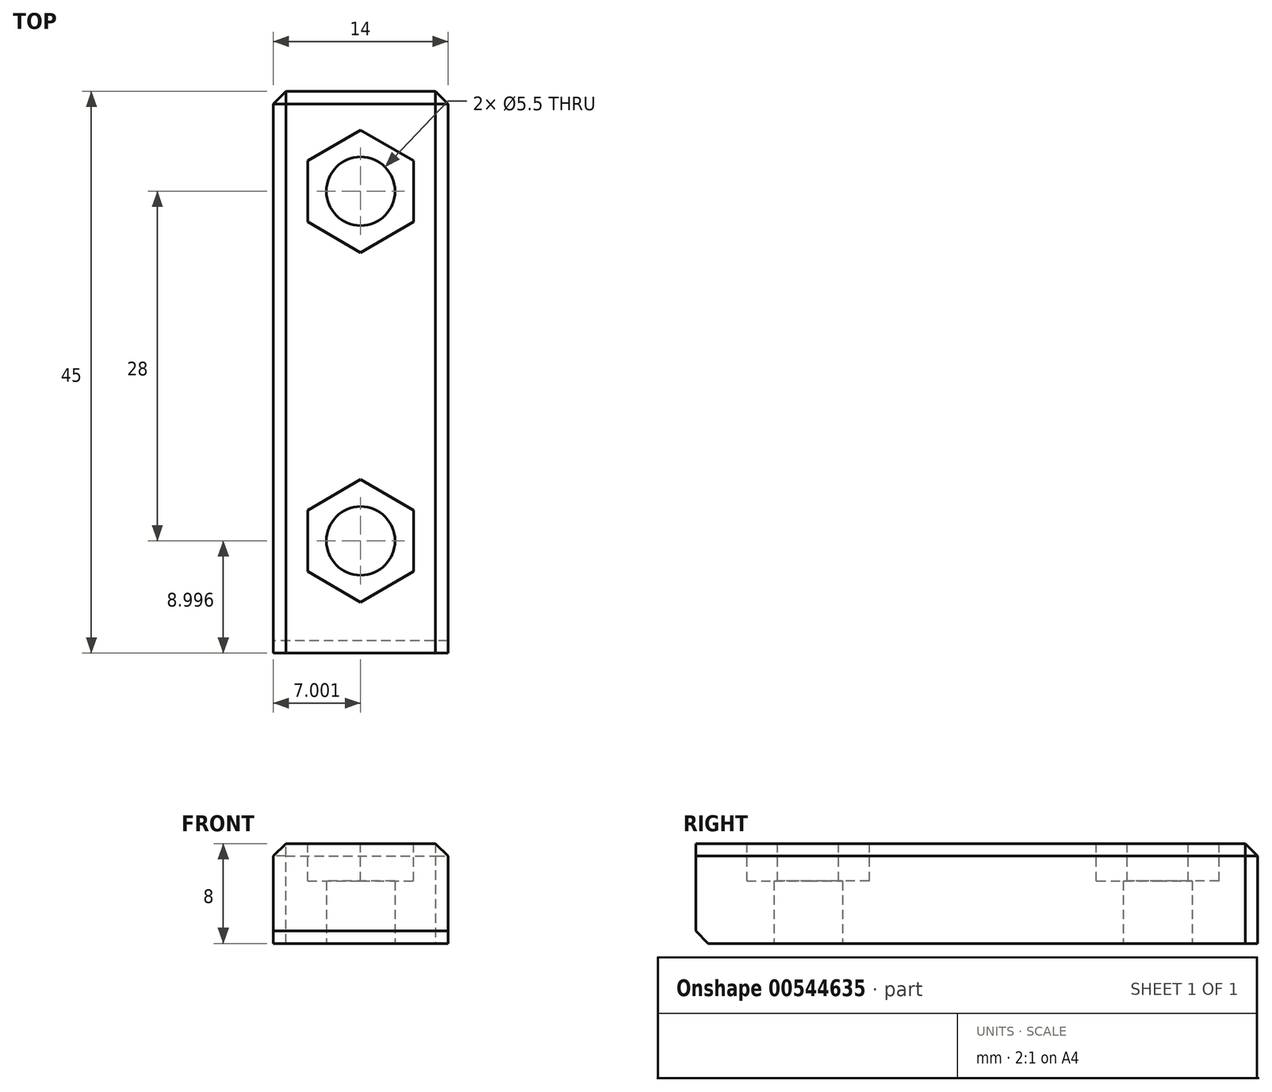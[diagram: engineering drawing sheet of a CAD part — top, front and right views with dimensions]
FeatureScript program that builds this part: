
annotation { "Feature Type Name" : "Feature", "Feature Type Description" : "" }
export const myFeature = defineFeature(function(context is Context, id is Id, definition is map)
    precondition{}
    {
        {
            var Q0;
            Q0=qCreatedBy(makeId("Top.planeOp"),FACE);
            var sketch = newSketch(context, id + "F0", { "sketchPlane" : qUnion([Q0])});
            skLineSegment(sketch, "E0.bottom", {"start": v(-22.78, 37.96) * mm, "end": v(-8.78, 37.96) * mm});
            skLineSegment(sketch, "E0.top", {"start": v(-22.78, -7.04) * mm, "end": v(-8.78, -7.04) * mm});
            skLineSegment(sketch, "E0.left", {"start": v(-22.78, 37.96) * mm, "end": v(-22.78, -7.04) * mm});
            skLineSegment(sketch, "E0.right", {"start": v(-8.78, 37.96) * mm, "end": v(-8.78, -7.04) * mm});
            skPoint(sketch, "E1", {"position": v(-15.78, -7.04) * mm});
            skCircle(sketch, "E2", {"center": v(-15.78, 1.96) * mm, "radius": 2.75 * mm});
            skCircle(sketch, "E3", {"center": v(-15.78, 29.96) * mm, "radius": 2.75 * mm});
            skSolve(sketch);
        }
        {
            var Q0;
            Q0=makeQuery(id+"F0.imprint","IMPRINT",FACE,{"disambiguationData":[TD([[makeQuery(id+"F0.imprint","IMPRINT",EDGE,{"derivedFrom":sQuery(id+"F0.wireOp",EDGE,"E0.bottom")}),-1.0]])]});
            extrude(context, id + "F1", {"entities" : qUnion([Q0]), "depth" : 8 * mm, "offsetDistance" : 25 * mm});
        }
        {
            var Q0;
            Q0=makeQuery(id+"F1.opExtrude","CAP_FACE",FACE,{"disambiguationData":[OSD([sQuery(id+"F0.wireOp",EDGE,"E0.bottom"),sQuery(id+"F0.wireOp",EDGE,"E0.top"),sQuery(id+"F0.wireOp",EDGE,"E0.left"),sQuery(id+"F0.wireOp",EDGE,"E0.right"),sQuery(id+"F0.wireOp",EDGE,"E2"),sQuery(id+"F0.wireOp",EDGE,"E3")])],"isStart":false});
            var sketch = newSketch(context, id + "F2", { "sketchPlane" : qUnion([Q0])});
            skCircle(sketch, "E4.cCircle", {"center": v(-15.78, 29.96) * mm, "radius": 4.25 * mm, "construction": true});
            skLineSegment(sketch, "E4.0", {"start": v(-11.53, 32.41) * mm, "end": v(-11.53, 27.5) * mm});
            skLineSegment(sketch, "E4.1", {"start": v(-11.53, 27.5) * mm, "end": v(-15.78, 25.05) * mm});
            skLineSegment(sketch, "E4.2", {"start": v(-15.78, 25.05) * mm, "end": v(-20.03, 27.5) * mm});
            skLineSegment(sketch, "E4.3", {"start": v(-20.03, 27.5) * mm, "end": v(-20.03, 32.41) * mm});
            skLineSegment(sketch, "E4.4", {"start": v(-20.03, 32.41) * mm, "end": v(-15.78, 34.86) * mm});
            skLineSegment(sketch, "E4.5", {"start": v(-15.78, 34.86) * mm, "end": v(-11.53, 32.41) * mm});
            skPoint(sketch, "E4.0.midPoint", {"position": v(-11.53, 29.96) * mm});
            skCircle(sketch, "E5.cCircle", {"center": v(-15.78, 1.96) * mm, "radius": 4.25 * mm, "construction": true});
            skLineSegment(sketch, "E5.0", {"start": v(-11.53, 4.41) * mm, "end": v(-11.53, -0.5) * mm});
            skLineSegment(sketch, "E5.1", {"start": v(-11.53, -0.5) * mm, "end": v(-15.78, -2.95) * mm});
            skLineSegment(sketch, "E5.2", {"start": v(-15.78, -2.95) * mm, "end": v(-20.03, -0.5) * mm});
            skLineSegment(sketch, "E5.3", {"start": v(-20.03, -0.5) * mm, "end": v(-20.03, 4.41) * mm});
            skLineSegment(sketch, "E5.4", {"start": v(-20.03, 4.41) * mm, "end": v(-15.78, 6.86) * mm});
            skLineSegment(sketch, "E5.5", {"start": v(-15.78, 6.86) * mm, "end": v(-11.53, 4.41) * mm});
            skPoint(sketch, "E5.0.midPoint", {"position": v(-11.53, 1.96) * mm});
            skSolve(sketch);
        }
        {
            var Q0;
            Q0 = qSketchRegion(id + "F2", true);
            extrude(context, id + "F3", {"entities" : qUnion([Q0]), "operationType" : NewBodyOperationType.REMOVE, "oppositeDirection" : true, "depth" : 3 * mm, "offsetDistance" : 25 * mm});
        }
        {
            var Q0;
            Q0=makeQuery(id+"F1.opExtrude","CAP_EDGE",EDGE,{"disambiguationData":[OSD([sQuery(id+"F0.wireOp",EDGE,"E0.bottom")])],"isStart":false});
            var Q1;
            Q1=makeQuery(id+"F1.opExtrude","SWEPT_EDGE",EDGE,{"disambiguationData":[OSD([sQuery(id+"F0.wireOp",EDGE,"E0.bottom"),sQuery(id+"F0.wireOp",EDGE,"E0.right")])]});
            var Q2;
            Q2=makeQuery(id+"F1.opExtrude","SWEPT_EDGE",EDGE,{"disambiguationData":[OSD([sQuery(id+"F0.wireOp",EDGE,"E0.bottom"),sQuery(id+"F0.wireOp",EDGE,"E0.left")])]});
            var Q3;
            Q3=makeQuery(id+"F1.opExtrude","CAP_EDGE",EDGE,{"disambiguationData":[OSD([sQuery(id+"F0.wireOp",EDGE,"E0.top")])],"isStart":true});
            var Q4;
            Q4=makeQuery(id+"F1.opExtrude","CAP_EDGE",EDGE,{"disambiguationData":[OSD([sQuery(id+"F0.wireOp",EDGE,"E0.right")])],"isStart":false});
            var Q5;
            Q5=makeQuery(id+"F1.opExtrude","CAP_EDGE",EDGE,{"disambiguationData":[OSD([sQuery(id+"F0.wireOp",EDGE,"E0.left")])],"isStart":false});
            chamfer(context, id + "F4", {"entities" : qUnion([Q0, Q1, Q2, Q3, Q4, Q5]), "width" : 1 * mm, "tangentPropagation" : true});
        }
    });
